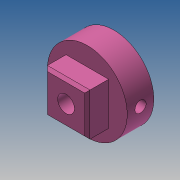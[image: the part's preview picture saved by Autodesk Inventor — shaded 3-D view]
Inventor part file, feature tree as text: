
AUTODESK INVENTOR PART (.ipt)
format: ipt  version: 2017 (Build 210142000, 142)  size: 184,832 bytes
history: native  units: mm
features: extrude x4, sketch x3, chamfer x2, other x1, projected_geometry x1
ambient origin geometry x8: Origin, YZ Plane, XZ Plane, XY Plane, X Axis, Y Axis, Z Axis, Center Point
bodies: Body1 (feature_tree)
feature tree (11):
  other  "Sólido1"
  extrude  "Extrusión1"  Depth=11.85mm
  sketch  "Boceto2"  dims[d3=6.650287mm d4=3.7mm]
  extrude  "Extrusión2"  Depth=3.7mm
  extrude  "Extrusión3"  Depth=16.0mm
  extrude  "Extrusión4"  TaperAngle=120.0deg  [1 undecoded]
  chamfer  "Chaflán1"  Distance=3.9mm
  chamfer  "Chaflán3"  Distance=16.0mm
  sketch  "Boceto1"  dims[d0=6.3mm d2=11.85mm]
  projected_geometry  "Contorno proyectado1"
  sketch  "Boceto3"  dims[d5=10.0mm d6=0.0mm d7=4.2mm d8=120.0deg d9=3.9mm d10=16.0mm d11=0.0mm d12=4.0mm d13=0.0mm d14=8.0mm d15=0.0mm d16=30.0mm d18=360.0deg d23=1.0mm d24=2.0mm d25=45.0deg d26=30.0mm d27=4.075mm d28=4.075mm d32=16.0mm d33=55.0mm d36=1.0mm d37=2.0mm d38=45.0deg]
note: 1 required parameter value undecoded (feature->parameter linkage not recoverable at this tier; creation-order binding heuristic only, values carry confidence <= 0.55)
